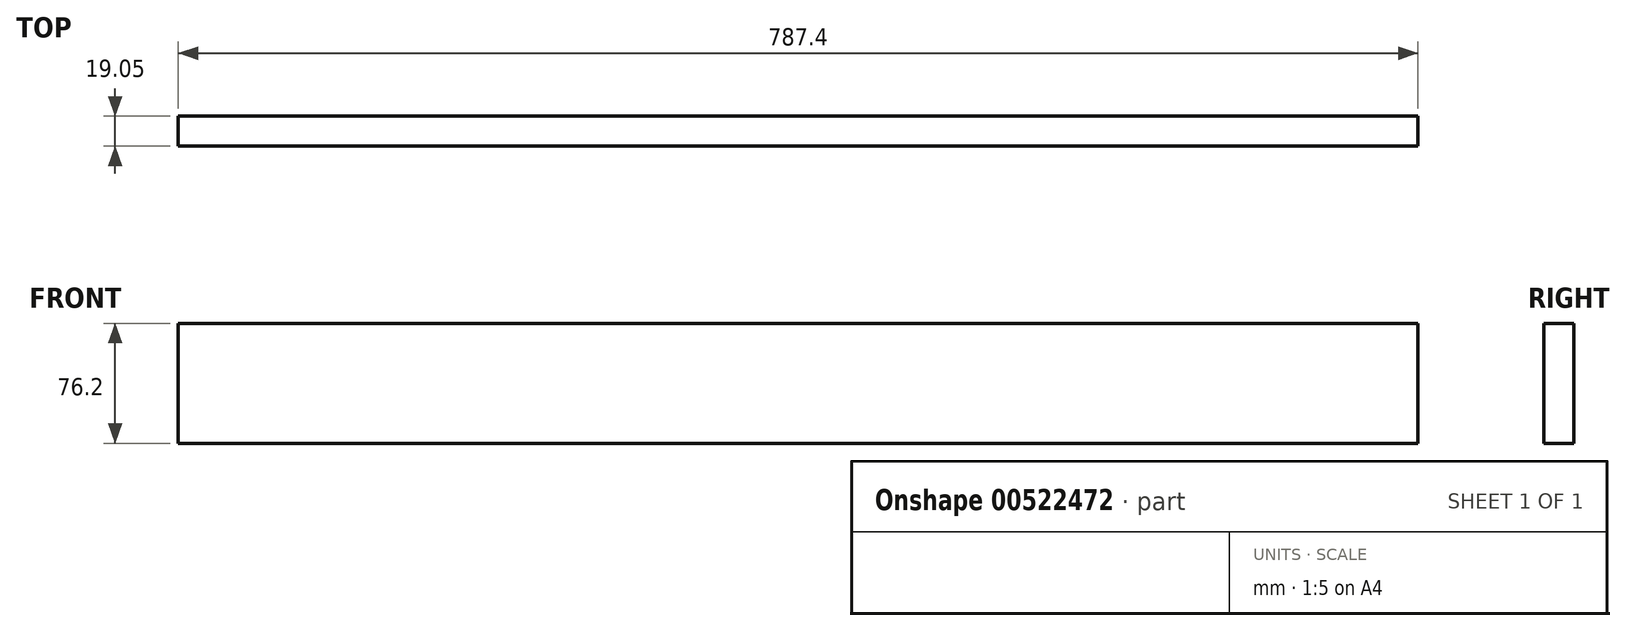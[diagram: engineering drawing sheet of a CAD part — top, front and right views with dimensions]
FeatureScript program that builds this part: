
annotation { "Feature Type Name" : "Feature", "Feature Type Description" : "" }
export const myFeature = defineFeature(function(context is Context, id is Id, definition is map)
    precondition{}
    {
        {
            var Q0;
            Q0=qCreatedBy(makeId("Top.planeOp"),FACE);
            var sketch = newSketch(context, id + "F0", { "sketchPlane" : qUnion([Q0])});
            skLineSegment(sketch, "E0.bottom", {"start": v(-253.72, -29.25) * mm, "end": v(533.68, -29.25) * mm});
            skLineSegment(sketch, "E0.top", {"start": v(-253.72, -48.3) * mm, "end": v(533.68, -48.3) * mm});
            skLineSegment(sketch, "E0.left", {"start": v(-253.72, -29.25) * mm, "end": v(-253.72, -48.3) * mm});
            skLineSegment(sketch, "E0.right", {"start": v(533.68, -29.25) * mm, "end": v(533.68, -48.3) * mm});
            skSolve(sketch);
        }
        {
            var Q0;
            Q0=makeQuery(id+"F0.imprint","IMPRINT",FACE,{"disambiguationData":[TD([[makeQuery(id+"F0.imprint","IMPRINT",EDGE,{"derivedFrom":sQuery(id+"F0.wireOp",EDGE,"E0.bottom")}),-1.0]])]});
            extrude(context, id + "F1", {"entities" : qUnion([Q0]), "depth" : 76.2 * mm, "offsetDistance" : 25.4 * mm});
        }
    });
